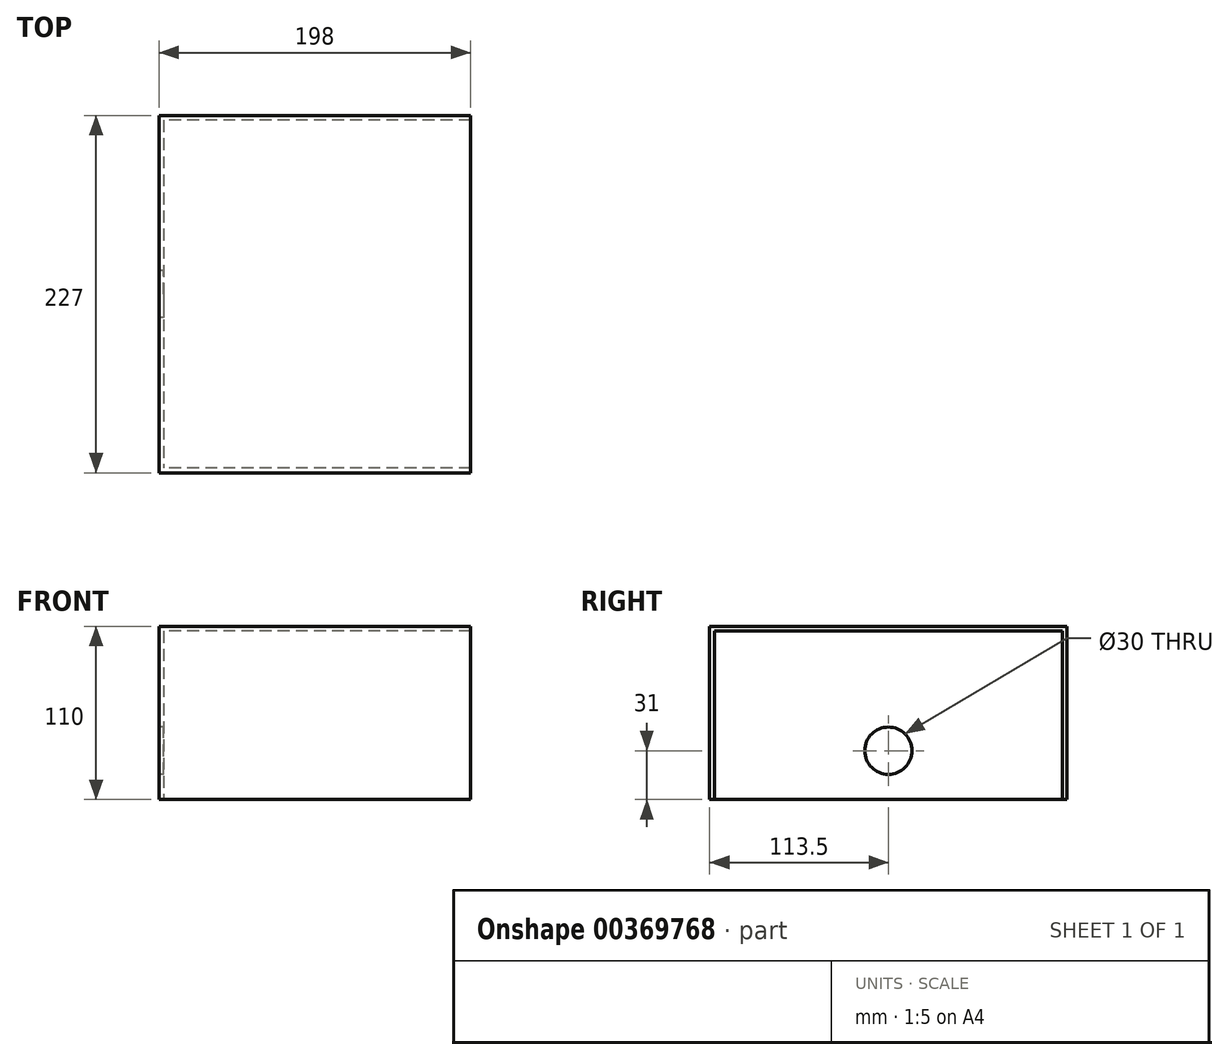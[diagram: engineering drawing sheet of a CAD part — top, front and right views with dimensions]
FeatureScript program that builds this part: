
annotation { "Feature Type Name" : "Feature", "Feature Type Description" : "" }
export const myFeature = defineFeature(function(context is Context, id is Id, definition is map)
    precondition{}
    {
        {
            var Q0;
            Q0=qCreatedBy(makeId("Right.planeOp"),FACE);
            var sketch = newSketch(context, id + "F0", { "sketchPlane" : qUnion([Q0])});
            skLineSegment(sketch, "E0.bottom", {"start": v(0, 0) * mm, "end": v(-227, 0) * mm});
            skLineSegment(sketch, "E0.top", {"start": v(0, 110) * mm, "end": v(-227, 110) * mm});
            skLineSegment(sketch, "E0.left", {"start": v(0, 0) * mm, "end": v(0, 110) * mm});
            skLineSegment(sketch, "E0.right", {"start": v(-227, 0) * mm, "end": v(-227, 110) * mm});
            skSolve(sketch);
        }
        {
            var Q0;
            Q0=makeQuery(id+"F0.imprint","IMPRINT",FACE,{"disambiguationData":[TD([[makeQuery(id+"F0.imprint","IMPRINT",EDGE,{"derivedFrom":sQuery(id+"F0.wireOp",EDGE,"E0.bottom")}),-1.0]])]});
            extrude(context, id + "F1", {"entities" : qUnion([Q0]), "depth" : 3 * mm});
        }
        {
            var Q0;
            Q0=makeQuery(id+"F1.opExtrude","CAP_FACE",FACE,{"disambiguationData":[OSD([sQuery(id+"F0.wireOp",EDGE,"E0.bottom"),sQuery(id+"F0.wireOp",EDGE,"E0.top"),sQuery(id+"F0.wireOp",EDGE,"E0.left"),sQuery(id+"F0.wireOp",EDGE,"E0.right")])],"isStart":false});
            var sketch = newSketch(context, id + "F2", { "sketchPlane" : qUnion([Q0])});
            skLineSegment(sketch, "E1.0.0", {"start": v(0, 0) * mm, "end": v(0, 110) * mm});
            skLineSegment(sketch, "E1.0.1", {"start": v(0, 110) * mm, "end": v(-227, 110) * mm});
            skLineSegment(sketch, "E1.0.2", {"start": v(-227, 110) * mm, "end": v(-227, 0) * mm});
            skLineSegment(sketch, "E1.0.3", {"start": v(-227, 0) * mm, "end": v(0, 0) * mm});
            skLineSegment(sketch, "E2", {"start": v(-227, 0) * mm, "end": v(-224, 0) * mm});
            skLineSegment(sketch, "E3", {"start": v(-224, 0) * mm, "end": v(-224, 107) * mm});
            skLineSegment(sketch, "E4", {"start": v(-224, 107) * mm, "end": v(-3, 107) * mm});
            skLineSegment(sketch, "E5", {"start": v(-3, 107) * mm, "end": v(-3, 0) * mm});
            skLineSegment(sketch, "E6", {"start": v(-3, 0) * mm, "end": v(0, 0) * mm});
            skSolve(sketch);
        }
        {
            var Q0;
            Q0=makeQuery(id+"F2.imprint","IMPRINT",FACE,{"disambiguationData":[TD([[makeQuery(id+"F2.imprint","IMPRINT",EDGE,{"derivedFrom":sQuery(id+"F2.wireOp",EDGE,"E1.0.0")}),1.0]])]});
            extrude(context, id + "F3", {"entities" : qUnion([Q0]), "operationType" : NewBodyOperationType.ADD, "depth" : 195 * mm});
        }
        {
            var Q0;
            Q0=makeQuery(id+"F1.opExtrude","CAP_FACE",FACE,{"disambiguationData":[OSD([sQuery(id+"F0.wireOp",EDGE,"E0.bottom"),sQuery(id+"F0.wireOp",EDGE,"E0.top"),sQuery(id+"F0.wireOp",EDGE,"E0.left"),sQuery(id+"F0.wireOp",EDGE,"E0.right")])],"isStart":true});
            var sketch = newSketch(context, id + "F4", { "sketchPlane" : qUnion([Q0])});
            skCircle(sketch, "E7", {"center": v(113.5, 31) * mm, "radius": 15 * mm});
            skSolve(sketch);
        }
        {
            var Q0;
            Q0=makeQuery(id+"F4.imprint","IMPRINT",FACE,{"disambiguationData":[TD([[makeQuery(id+"F4.imprint","IMPRINT",EDGE,{"derivedFrom":sQuery(id+"F4.wireOp",EDGE,"E7")}),1.0]])]});
            extrude(context, id + "F5", {"entities" : qUnion([Q0]), "operationType" : NewBodyOperationType.REMOVE, "oppositeDirection" : true, "depth" : 25 * mm});
        }
    });
